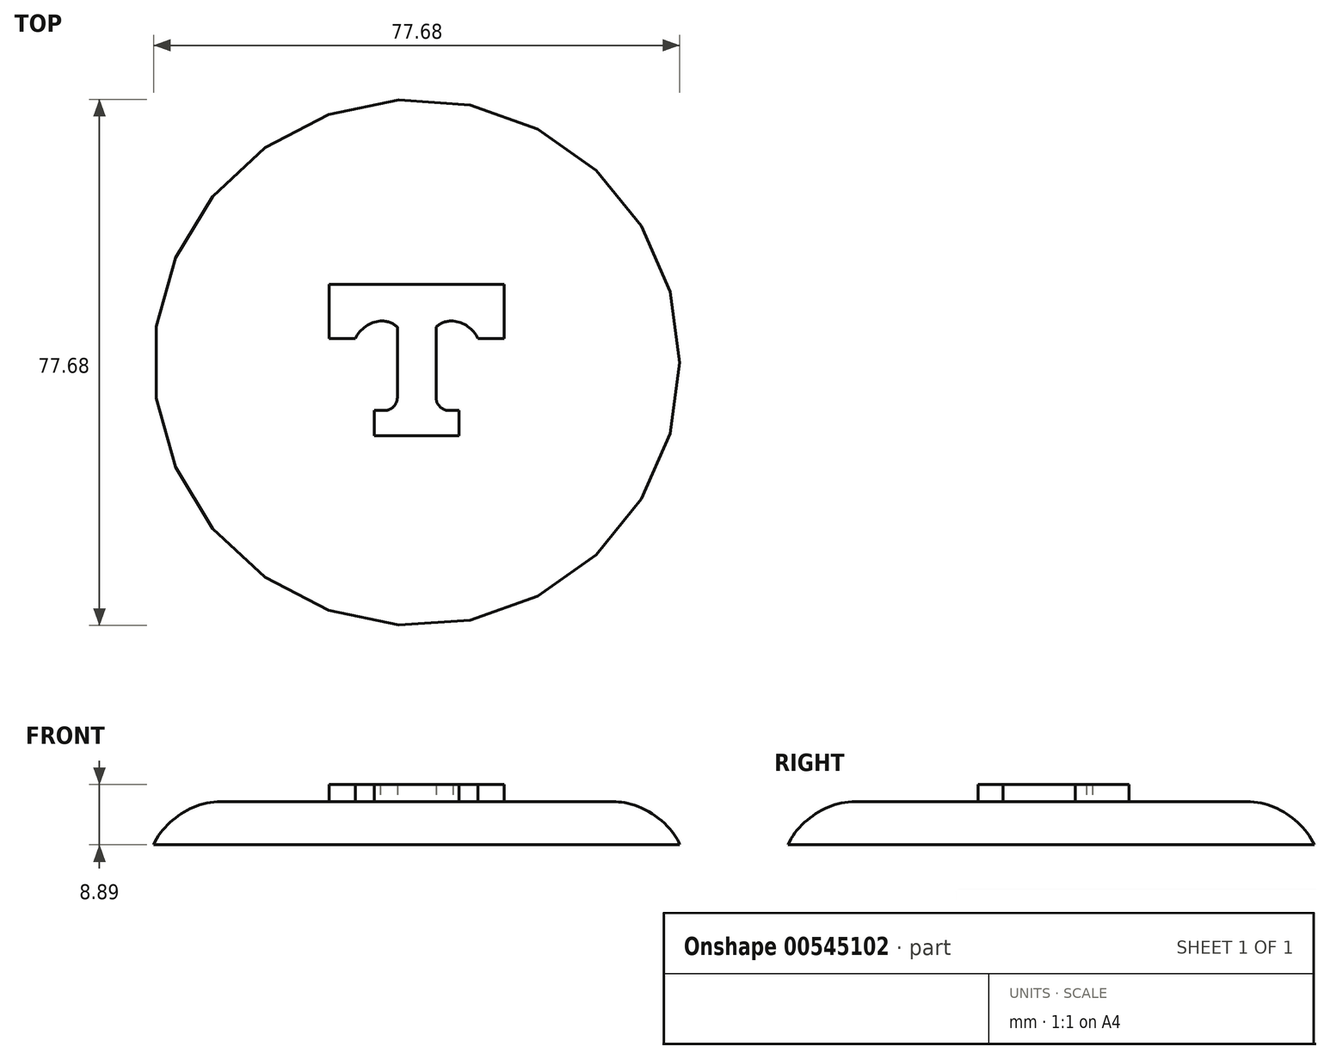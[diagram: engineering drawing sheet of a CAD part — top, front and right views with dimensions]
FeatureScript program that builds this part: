
annotation { "Feature Type Name" : "Feature", "Feature Type Description" : "" }
export const myFeature = defineFeature(function(context is Context, id is Id, definition is map)
    precondition{}
    {
        {
            var Q0;
            Q0=qCreatedBy(makeId("Top.planeOp"),FACE);
            var sketch = newSketch(context, id + "F0", { "sketchPlane" : qUnion([Q0])});
            skCircle(sketch, "E0", {"center": v(0, 0) * mm, "radius": 38.84 * mm});
            skSolve(sketch);
        }
        {
            var Q0;
            Q0=makeQuery(id+"F0.imprint","IMPRINT",FACE,{"disambiguationData":[TD([[makeQuery(id+"F0.imprint","IMPRINT",EDGE,{"derivedFrom":sQuery(id+"F0.wireOp",EDGE,"E0")}),1.0]])]});
            extrude(context, id + "F1", {"entities" : qUnion([Q0]), "depth" : 6.35 * mm, "offsetDistance" : 25.4 * mm});
        }
        {
            var Q0;
            Q0=makeQuery(id+"F1.opExtrude","CAP_FACE",FACE,{"disambiguationData":[OSD([sQuery(id+"F0.wireOp",EDGE,"E0")])],"isStart":false});
            fillet(context, id + "F2", {"entities" : qUnion([Q0]), "radius" : 10.16 * mm, "tangentPropagation" : true, "rho" : .4, "crossSection" : FilletCrossSection.CONIC, "allowEdgeOverflow" : false});
        }
        {
            var Q0;
            Q0=makeQuery(id+"F1.opExtrude","CAP_FACE",FACE,{"disambiguationData":[OSD([sQuery(id+"F0.wireOp",EDGE,"E0")])],"isStart":false});
            var sketch = newSketch(context, id + "F3", { "sketchPlane" : qUnion([Q0])});
            skSolve(sketch);
        }
        {
            var Q0;
            {var subQ0=sQuery(id+"F0.wireOp",EDGE,"E0");Q0=makeQuery(id+"F3.imprint","IMPRINT",FACE,{"disambiguationData":[TD([[makeQuery(id+"F3.imprint","IMPRINT",EDGE,{"derivedFrom":makeQuery(id+"F2.opFillet","BLEND_EDGE",EDGE,{"blendedFrom":[makeQuery(id+"F1.opExtrude","CAP_EDGE",EDGE,{"disambiguationData":[OSD([subQ0])],"isStart":false}),makeQuery(id+"F1.opExtrude","CAP_FACE",FACE,{"disambiguationData":[OSD([subQ0])],"isStart":false})],"blendedInto":[makeQuery(id+"F1.opExtrude","CAP_FACE",FACE,{"disambiguationData":[OSD([subQ0])],"isStart":false})]})}),1.0]])]});}
            var sketch = newSketch(context, id + "F4", { "sketchPlane" : qUnion([Q0])});
            skArc(sketch, "E1", {"start": v(-5.36, 6.13) * mm, "mid": v(-7.55, 5.31) * mm, "end": v(-9.07, 3.55) * mm});
            skArc(sketch, "E2", {"start": v(-2.86, 5.24) * mm, "mid": v(-4.02, 5.93) * mm, "end": v(-5.36, 6.13) * mm});
            skArc(sketch, "E3.MirrorCS", {"start": v(2.86, 5.24) * mm, "mid": v(4.02, 5.93) * mm, "end": v(5.36, 6.13) * mm});
            skArc(sketch, "E4.MirrorCS", {"start": v(5.36, 6.13) * mm, "mid": v(7.55, 5.31) * mm, "end": v(9.07, 3.55) * mm});
            skLineSegment(sketch, "E5", {"start": v(-2.86, 5.24) * mm, "end": v(-2.86, -5.17) * mm});
            skArc(sketch, "E6", {"start": v(-4.8, -7.1) * mm, "mid": v(-3.43, -6.54) * mm, "end": v(-2.86, -5.17) * mm});
            skLineSegment(sketch, "E7", {"start": v(-4.8, -7.1) * mm, "end": v(-6.27, -7.1) * mm});
            skLineSegment(sketch, "E8", {"start": v(-6.27, -7.1) * mm, "end": v(-6.27, -10.79) * mm});
            skLineSegment(sketch, "E9", {"start": v(-6.27, -10.79) * mm, "end": v(0, -10.79) * mm});
            skLineSegment(sketch, "E10.MirrorCS", {"start": v(6.27, -10.79) * mm, "end": v(0, -10.79) * mm});
            skLineSegment(sketch, "E11.MirrorCS", {"start": v(6.27, -7.1) * mm, "end": v(6.27, -10.79) * mm});
            skLineSegment(sketch, "E12.MirrorCS", {"start": v(2.86, 5.24) * mm, "end": v(2.86, -5.17) * mm});
            skArc(sketch, "E13.MirrorCS", {"start": v(4.8, -7.1) * mm, "mid": v(3.43, -6.54) * mm, "end": v(2.86, -5.17) * mm});
            skLineSegment(sketch, "E14.MirrorCS", {"start": v(4.8, -7.1) * mm, "end": v(6.27, -7.1) * mm});
            skLineSegment(sketch, "E15", {"start": v(-9.07, 3.55) * mm, "end": v(-12.93, 3.55) * mm});
            skLineSegment(sketch, "E16", {"start": v(-12.93, 3.55) * mm, "end": v(-12.93, 11.53) * mm});
            skLineSegment(sketch, "E17", {"start": v(-12.93, 11.53) * mm, "end": v(0, 11.53) * mm});
            skLineSegment(sketch, "E18.MirrorCS", {"start": v(9.07, 3.55) * mm, "end": v(12.93, 3.55) * mm});
            skLineSegment(sketch, "E19.MirrorCS", {"start": v(12.93, 3.55) * mm, "end": v(12.93, 11.53) * mm});
            skLineSegment(sketch, "E20.MirrorCS", {"start": v(12.93, 11.53) * mm, "end": v(0, 11.53) * mm});
            skSolve(sketch);
        }
        {
            var Q0;
            Q0 = qSketchRegion(id + "F4", true);
            extrude(context, id + "F5", {"entities" : qUnion([Q0]), "operationType" : NewBodyOperationType.ADD, "depth" : 2.54 * mm, "offsetDistance" : 25.4 * mm});
        }
    });
